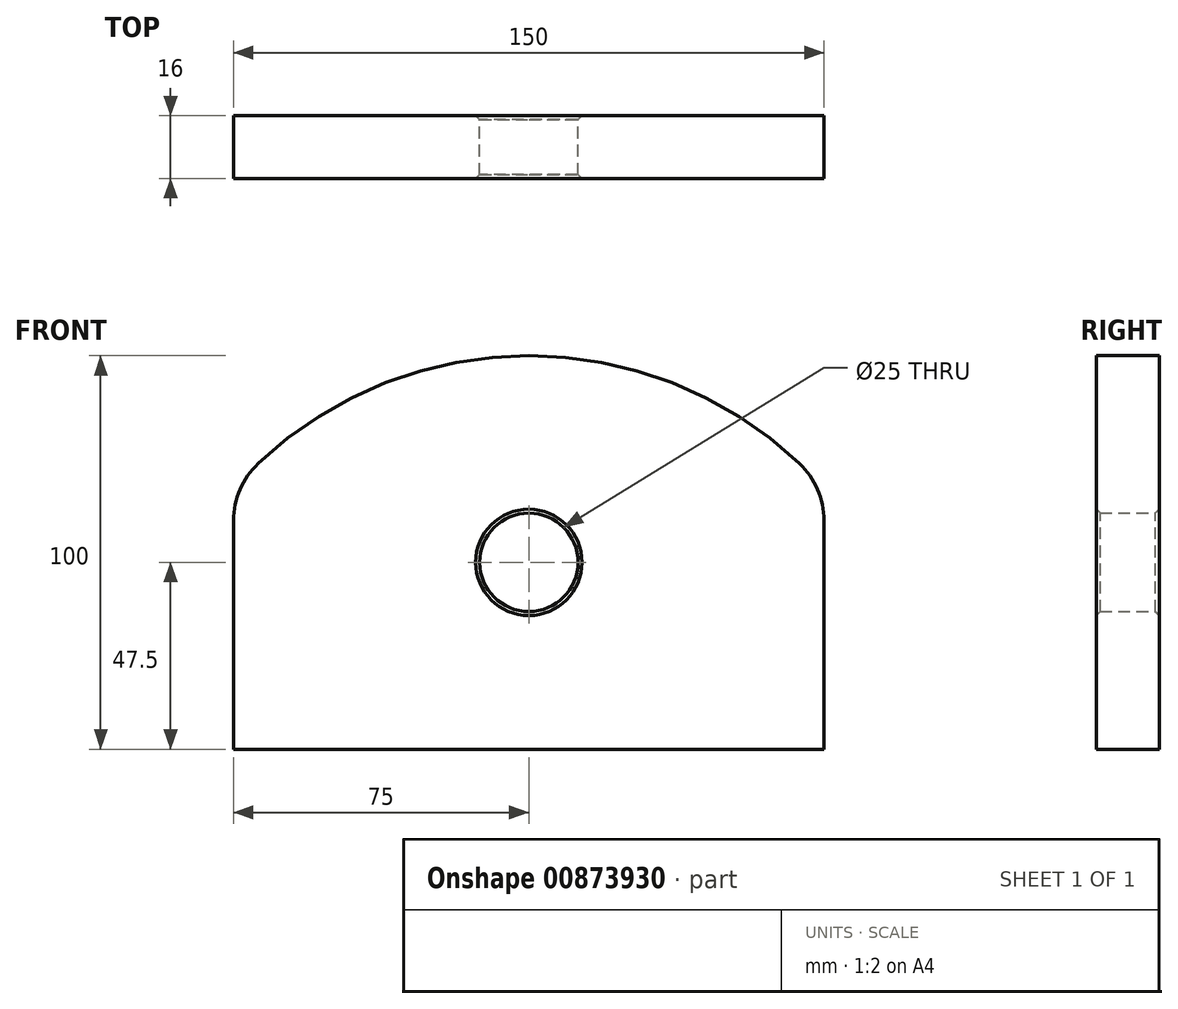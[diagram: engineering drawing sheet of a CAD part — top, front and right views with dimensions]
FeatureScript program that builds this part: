
annotation { "Feature Type Name" : "Feature", "Feature Type Description" : "" }
export const myFeature = defineFeature(function(context is Context, id is Id, definition is map)
    precondition{}
    {
        {
            var Q0;
            Q0=qCreatedBy(makeId("Front.planeOp"),FACE);
            var sketch = newSketch(context, id + "F0", { "sketchPlane" : qUnion([Q0])});
            skCircle(sketch, "E0", {"center": v(0, 0) * mm, "radius": 12.5 * mm});
            skLineSegment(sketch, "E1", {"start": v(0, -12.5) * mm, "end": v(0, -47.5) * mm, "construction": true});
            skLineSegment(sketch, "E2", {"start": v(0, 12.5) * mm, "end": v(0, 52.5) * mm, "construction": true});
            skLineSegment(sketch, "E3", {"start": v(-75, -47.5) * mm, "end": v(75, -47.5) * mm});
            skArc(sketch, "E4", {"start": v(68.75, 25.12) * mm, "mid": v(0, 52.5) * mm, "end": v(-68.75, 25.12) * mm});
            skLineSegment(sketch, "E5", {"start": v(-75, -47.5) * mm, "end": v(-75, 10.6) * mm});
            skLineSegment(sketch, "E6", {"start": v(75, -47.5) * mm, "end": v(75, 10.6) * mm});
            skPoint(sketch, "E7.visualSharp", {"position": v(-75, 18.64) * mm});
            skArc(sketch, "E7.filletArc", {"start": v(-68.75, 25.12) * mm, "mid": v(-73.37, 18.5) * mm, "end": v(-75, 10.6) * mm});
            skPoint(sketch, "E8.visualSharp", {"position": v(75, 18.64) * mm});
            skArc(sketch, "E8.filletArc", {"start": v(75, 10.6) * mm, "mid": v(73.37, 18.5) * mm, "end": v(68.75, 25.12) * mm});
            skSolve(sketch);
        }
        {
            var Q0;
            Q0=makeQuery(id+"F0.imprint","IMPRINT",FACE,{"disambiguationData":[TD([[makeQuery(id+"F0.imprint","IMPRINT",EDGE,{"derivedFrom":sQuery(id+"F0.wireOp",EDGE,"E0")}),-1.0]])]});
            extrude(context, id + "F1", {"entities" : qUnion([Q0]), "depth" : 16 * mm, "offsetDistance" : 25 * mm, "symmetric" : true});
        }
        {
            var Q0;
            Q0=makeQuery(id+"F1.opExtrude","CAP_EDGE",EDGE,{"disambiguationData":[OSD([sQuery(id+"F0.wireOp",EDGE,"E0")])],"isStart":false});
            var Q1;
            Q1=makeQuery(id+"F1.opExtrude","CAP_EDGE",EDGE,{"disambiguationData":[OSD([sQuery(id+"F0.wireOp",EDGE,"E0")])],"isStart":true});
            chamfer(context, id + "F2", {"entities" : qUnion([Q0, Q1]), "width" : 1 * mm, "tangentPropagation" : true});
        }
    });
